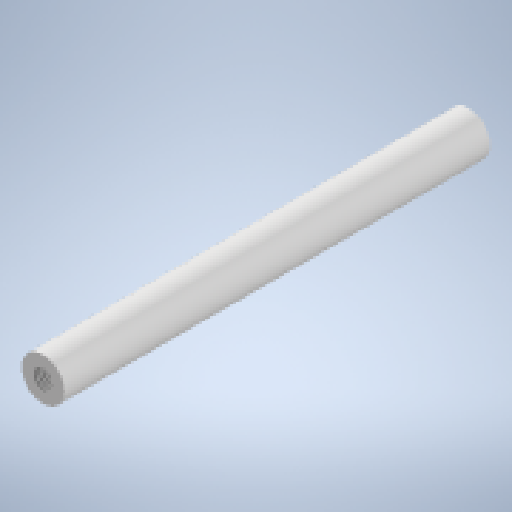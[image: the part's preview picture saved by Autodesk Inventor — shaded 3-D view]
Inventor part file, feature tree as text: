
AUTODESK INVENTOR PART (.ipt)
format: ipt  version: 2023 (Build 270158000, 158)  size: 156,160 bytes
history: native  units: mm
features: extrude x3, sketch x3, thread x2
ambient origin geometry x8: Origin, YZ Plane, XZ Plane, XY Plane, X Axis, Y Axis, Z Axis, Center Point
bodies: Solid1 (feature_tree)
feature tree (8):
  extrude  "Extrusion1"  Depth=50.0mm TaperAngle=0.0deg
  extrude  "Extrusion2"  Depth=20.0mm TaperAngle=0.0deg
  extrude  "Extrusion3"  Depth=20.0mm TaperAngle=0.0deg
  thread  "Thread1"  [1 undecoded]
  thread  "Thread2"  [1 undecoded]
  sketch  "Sketch1"  dims[d0=5.0mm d1=50.0mm d2=0.0mm]
  sketch  "Sketch2"  dims[d3=2.2mm d4=20.0mm d5=0.0mm]
  sketch  "Sketch3"  dims[d6=20.0mm d7=0.0mm d8=16.0mm d9=0.0mm d10=16.0mm d11=0.0mm]
note: 2 required parameter values undecoded (feature->parameter linkage not recoverable at this tier; creation-order binding heuristic only, values carry confidence <= 0.55)
